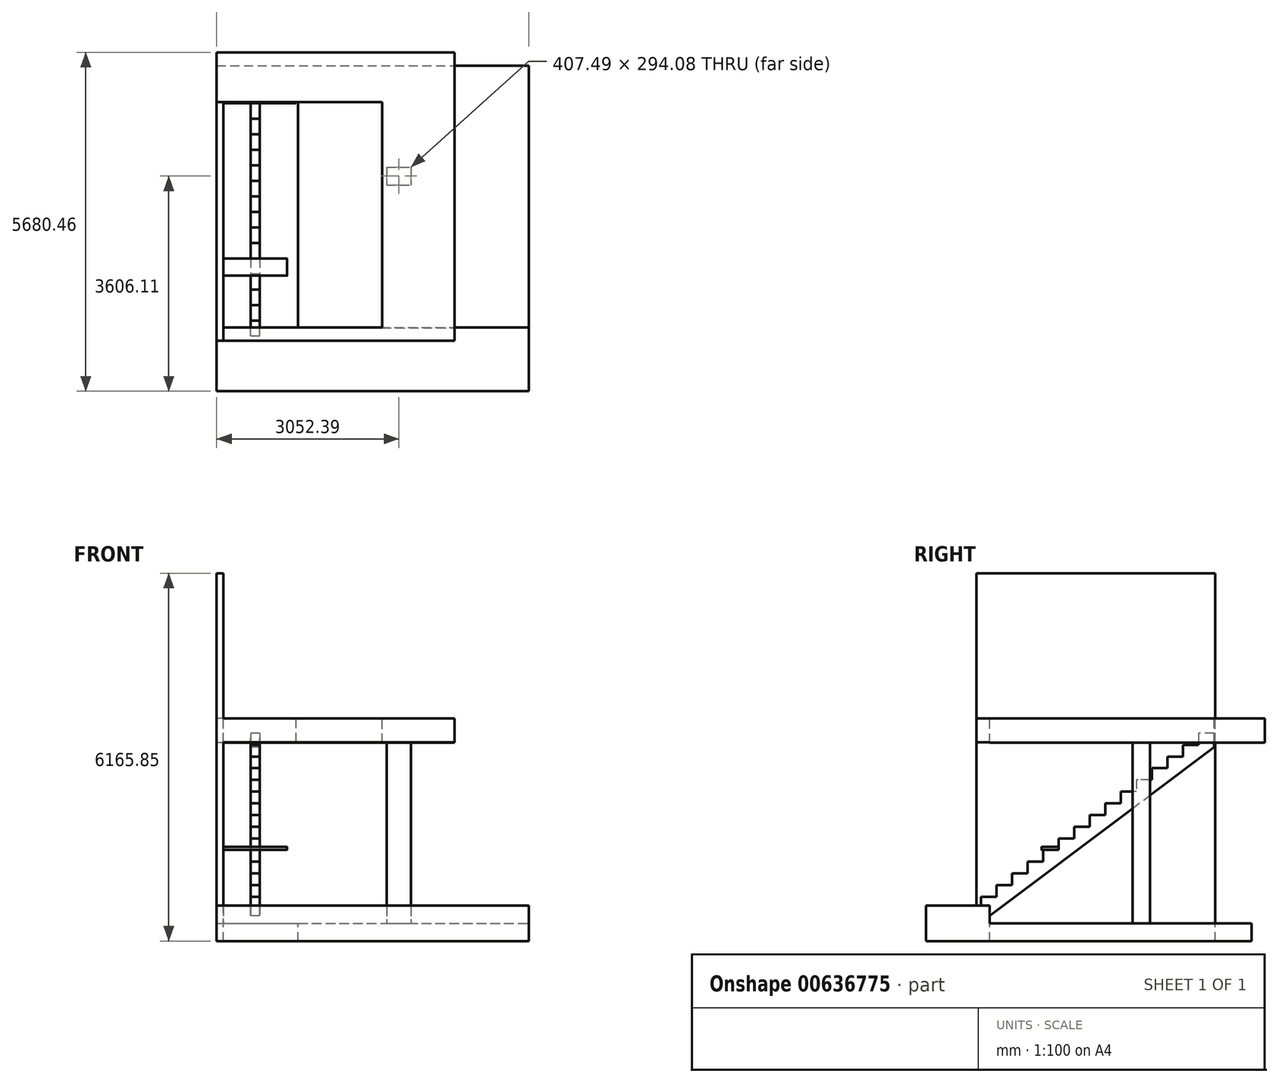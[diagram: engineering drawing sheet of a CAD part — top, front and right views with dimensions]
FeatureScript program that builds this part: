
annotation { "Feature Type Name" : "Feature", "Feature Type Description" : "" }
export const myFeature = defineFeature(function(context is Context, id is Id, definition is map)
    precondition{}
    {
        {
            var Q0;
            Q0=qCreatedBy(makeId("Top.planeOp"),FACE);
            var Q1;
            Q1 = qBodyType(qCreatedBy(id + "F1" ,EDGE), BodyType.WIRE);
            cPlane(context, id + "F0", {"entities" : qUnion([Q0, Q1]), "cplaneType" : CPlaneType.OFFSET, "offset" : 3432.17 * mm, "width" : 152.4 * mm, "height" : 152.4 * mm});
        }
        {
            var Q0;
            Q0=qCreatedBy(makeId("Top.planeOp"),FACE);
            var sketch = newSketch(context, id + "F1", { "sketchPlane" : qUnion([Q0])});
            skLineSegment(sketch, "E0.bottom", {"start": v(0, 0) * mm, "end": v(1250.95, 0) * mm});
            skLineSegment(sketch, "E0.top", {"start": v(0, 3778.25) * mm, "end": v(1250.95, 3778.25) * mm});
            skLineSegment(sketch, "E0.left", {"start": v(0, 0) * mm, "end": v(0, 3778.25) * mm});
            skLineSegment(sketch, "E0.right", {"start": v(1250.95, 0) * mm, "end": v(1250.95, 3778.25) * mm});
            skLineSegment(sketch, "E1.bottom", {"start": v(-114.3, -1066.8) * mm, "end": v(5114.93, -1066.8) * mm});
            skLineSegment(sketch, "E1.top", {"start": v(-114.3, 4387.85) * mm, "end": v(5114.93, 4387.85) * mm});
            skLineSegment(sketch, "E1.left", {"start": v(-114.3, -1066.8) * mm, "end": v(-114.3, 4387.85) * mm});
            skLineSegment(sketch, "E1.right", {"start": v(5114.93, -1066.8) * mm, "end": v(5114.93, 4387.85) * mm});
            skSolve(sketch);
        }
        {
            var Q0;
            Q0=makeQuery(id+"F1.imprint","IMPRINT",FACE,{"disambiguationData":[TD([[makeQuery(id+"F1.imprint","IMPRINT",EDGE,{"derivedFrom":sQuery(id+"F1.wireOp",EDGE,"E0.bottom")}),-1.0]])]});
            extrude(context, id + "F2", {"entities" : qUnion([Q0]), "oppositeDirection" : true, "depth" : 298.45 * mm, "offsetDistance" : 25.4 * mm});
        }
        {
            var Q0;
            Q0=makeQuery(id+"F1.imprint","IMPRINT",FACE,{"disambiguationData":[TD([[makeQuery(id+"F1.imprint","IMPRINT",EDGE,{"derivedFrom":sQuery(id+"F1.wireOp",EDGE,"E0.bottom")}),-1.0]])]});
            var sketch = newSketch(context, id + "F3", { "sketchPlane" : qUnion([Q0])});
            skLineSegment(sketch, "E2.bottom", {"start": v(-114.3, -1066.8) * mm, "end": v(5114.93, -1066.8) * mm});
            skLineSegment(sketch, "E2.top", {"start": v(-114.3, 0) * mm, "end": v(5114.93, 0) * mm});
            skLineSegment(sketch, "E2.left", {"start": v(-114.3, -1066.8) * mm, "end": v(-114.3, 0) * mm});
            skLineSegment(sketch, "E2.right", {"start": v(5114.93, -1066.8) * mm, "end": v(5114.93, 0) * mm});
            skSolve(sketch);
        }
        {
            var Q0;
            Q0=makeQuery(id+"F3.imprint","IMPRINT",FACE,{"disambiguationData":[TD([[makeQuery(id+"F3.imprint","IMPRINT",EDGE,{"derivedFrom":sQuery(id+"F3.wireOp",EDGE,"E2.bottom")}),1.0]])]});
            extrude(context, id + "F4", {"entities" : qUnion([Q0]), "operationType" : NewBodyOperationType.ADD, "depth" : 298.45 * mm, "offsetDistance" : 25.4 * mm});
        }
        {
            var Q0;
            Q0=qCreatedBy(id+"F0.planeOp",FACE);
            var sketch = newSketch(context, id + "F5", { "sketchPlane" : qUnion([Q0])});
            skLineSegment(sketch, "E3.top", {"start": v(0, 3778.25) * mm, "end": v(2660.65, 3778.25) * mm});
            skLineSegment(sketch, "E3.left", {"start": v(0, 0) * mm, "end": v(0, 3778.25) * mm});
            skLineSegment(sketch, "E4.bottom", {"start": v(-114.3, 0) * mm, "end": v(0, 0) * mm});
            skLineSegment(sketch, "E4.top", {"start": v(-114.3, 4613.66) * mm, "end": v(3863.97, 4613.66) * mm});
            skLineSegment(sketch, "E4.left", {"start": v(-114.3, 0) * mm, "end": v(-114.3, 4613.66) * mm});
            skLineSegment(sketch, "E5", {"start": v(2660.65, 3778.25) * mm, "end": v(2660.65, -1.59) * mm});
            skLineSegment(sketch, "E6", {"start": v(2660.65, -1.59) * mm, "end": v(3873.5, -1.59) * mm});
            skLineSegment(sketch, "E7", {"start": v(3873.5, -1.59) * mm, "end": v(3873.5, 4613.66) * mm});
            skLineSegment(sketch, "E8", {"start": v(3873.5, 4613.66) * mm, "end": v(3863.97, 4613.66) * mm});
            skSolve(sketch);
        }
        {
            var Q0;
            Q0 = qSketchRegion(id + "F5", true);
            extrude(context, id + "F6", {"entities" : qUnion([Q0]), "oppositeDirection" : true, "depth" : 404.8 * mm, "offsetDistance" : 25.4 * mm});
        }
        {
            var Q0;
            Q0=makeQuery(id+"F5.imprint","IMPRINT",FACE,{"disambiguationData":[TD([[makeQuery(id+"F5.imprint","IMPRINT",EDGE,{"derivedFrom":sQuery(id+"F5.wireOp",EDGE,"E3.top")}),1.0]])]});
            var sketch = newSketch(context, id + "F7", { "sketchPlane" : qUnion([Q0])});
            skLineSegment(sketch, "E9", {"start": v(-114.3, 0) * mm, "end": v(3873.5, 0) * mm});
            skLineSegment(sketch, "E10", {"start": v(3873.5, 0) * mm, "end": v(3873.5, -222.25) * mm});
            skLineSegment(sketch, "E11", {"start": v(3873.5, -222.25) * mm, "end": v(-114.3, -222.25) * mm});
            skLineSegment(sketch, "E12", {"start": v(-114.3, -222.25) * mm, "end": v(-114.3, 0) * mm});
            skSolve(sketch);
        }
        {
            var Q0;
            {var subQ2=sQuery(id+"F7.wireOp",EDGE,"E11");Q0=makeQuery(id+"F7.imprint","IMPRINT",FACE,{"disambiguationData":[TD([[makeQuery(id+"F7.imprint","IMPRINT",EDGE,{"derivedFrom":subQ2}),-1.0]])]});}
            extrude(context, id + "F8", {"entities" : qUnion([Q0]), "oppositeDirection" : true, "depth" : 400.05 * mm, "offsetDistance" : 25.4 * mm});
        }
        {
            var Q0;
            Q0=makeQuery(id+"F1.imprint","IMPRINT",FACE,{"disambiguationData":[TD([[makeQuery(id+"F1.imprint","IMPRINT",EDGE,{"derivedFrom":sQuery(id+"F1.wireOp",EDGE,"E0.bottom")}),-1.0]])]});
            var sketch = newSketch(context, id + "F9", { "sketchPlane" : qUnion([Q0])});
            skLineSegment(sketch, "E13.bottom", {"start": v(-114.3, 3778.25) * mm, "end": v(0, 3778.25) * mm});
            skLineSegment(sketch, "E13.top", {"start": v(-114.3, -222.25) * mm, "end": v(0, -222.25) * mm});
            skLineSegment(sketch, "E13.left", {"start": v(-114.3, 3778.25) * mm, "end": v(-114.3, -222.25) * mm});
            skLineSegment(sketch, "E13.right", {"start": v(0, 3778.25) * mm, "end": v(0, -222.25) * mm});
            skSolve(sketch);
        }
        {
            var Q0;
            Q0 = qSketchRegion(id + "F9", true);
            extrude(context, id + "F10", {"entities" : qUnion([Q0]), "operationType" : NewBodyOperationType.ADD, "depth" : 5867.4 * mm, "offsetDistance" : 25.4 * mm});
        }
        {
            var Q0;
            Q0=makeQuery(id+"F5.imprint","IMPRINT",FACE,{"disambiguationData":[TD([[makeQuery(id+"F5.imprint","IMPRINT",EDGE,{"derivedFrom":sQuery(id+"F5.wireOp",EDGE,"E3.top")}),1.0]])]});
            var sketch = newSketch(context, id + "F11", { "sketchPlane" : qUnion([Q0])});
            skLineSegment(sketch, "E14.bottom", {"start": v(0, 3778.25) * mm, "end": v(1219.2, 3778.25) * mm});
            skLineSegment(sketch, "E14.top", {"start": v(0, 3759.2) * mm, "end": v(1219.2, 3759.2) * mm});
            skLineSegment(sketch, "E14.left", {"start": v(0, 3778.25) * mm, "end": v(0, 3759.2) * mm});
            skLineSegment(sketch, "E14.right", {"start": v(1219.2, 3778.25) * mm, "end": v(1219.2, 3759.2) * mm});
            skSolve(sketch);
        }
        {
            var Q0;
            Q0 = qSketchRegion(id + "F11", true);
            extrude(context, id + "F12", {"entities" : qUnion([Q0]), "oppositeDirection" : true, "depth" : 391.16 * mm, "offsetDistance" : 25.4 * mm});
        }
        {
            var Q0;
            Q0=makeQuery(id+"F10.opExtrude","SWEPT_FACE",FACE,{"disambiguationData":[OSD([sQuery(id+"F9.wireOp",EDGE,"E13.right")])]});
            cPlane(context, id + "F13", {"entities" : qUnion([Q0]), "cplaneType" : CPlaneType.OFFSET, "offset" : 457.2 * mm, "width" : 152.4 * mm, "height" : 152.4 * mm});
        }
        {
            var Q0;
            Q0=qCreatedBy(id+"F13.planeOp",FACE);
            var sketch = newSketch(context, id + "F14", { "sketchPlane" : qUnion([Q0])});
            skLineSegment(sketch, "E15", {"start": v(3759.2, 3185.52) * mm, "end": v(3498.85, 3185.52) * mm});
            skLineSegment(sketch, "E16", {"start": v(3498.85, 3185.52) * mm, "end": v(3498.85, 2989.66) * mm});
            skLineSegment(sketch, "E17", {"start": v(3498.85, 2989.66) * mm, "end": v(3238.5, 2989.66) * mm});
            skLineSegment(sketch, "E18", {"start": v(3238.5, 2989.66) * mm, "end": v(3238.5, 2793.8) * mm});
            skLineSegment(sketch, "E19", {"start": v(3238.5, 2793.8) * mm, "end": v(2978.15, 2793.8) * mm});
            skLineSegment(sketch, "E20", {"start": v(2978.15, 2793.8) * mm, "end": v(2978.15, 2597.94) * mm});
            skLineSegment(sketch, "E21", {"start": v(2978.15, 2597.94) * mm, "end": v(2717.8, 2597.94) * mm});
            skLineSegment(sketch, "E22", {"start": v(2717.8, 2597.94) * mm, "end": v(2717.8, 2402.09) * mm});
            skLineSegment(sketch, "E23", {"start": v(2717.8, 2402.09) * mm, "end": v(2457.45, 2402.09) * mm});
            skLineSegment(sketch, "E24", {"start": v(2457.45, 2402.09) * mm, "end": v(2457.45, 2206.23) * mm});
            skLineSegment(sketch, "E25", {"start": v(2457.45, 2206.23) * mm, "end": v(2197.1, 2206.23) * mm});
            skLineSegment(sketch, "E26", {"start": v(2197.1, 2206.23) * mm, "end": v(2197.1, 2010.37) * mm});
            skLineSegment(sketch, "E27", {"start": v(2197.1, 2010.37) * mm, "end": v(1936.75, 2010.37) * mm});
            skLineSegment(sketch, "E28", {"start": v(1936.75, 2010.37) * mm, "end": v(1936.75, 1814.51) * mm});
            skLineSegment(sketch, "E29", {"start": v(1936.75, 1814.51) * mm, "end": v(1676.4, 1814.51) * mm});
            skLineSegment(sketch, "E30", {"start": v(1676.4, 1814.51) * mm, "end": v(1676.4, 1618.65) * mm});
            skLineSegment(sketch, "E31", {"start": v(1676.4, 1618.65) * mm, "end": v(1416.05, 1618.65) * mm});
            skLineSegment(sketch, "E32", {"start": v(1416.05, 1618.65) * mm, "end": v(1416.05, 1422.8) * mm});
            skLineSegment(sketch, "E33", {"start": v(1416.05, 1422.8) * mm, "end": v(1155.7, 1422.8) * mm});
            skLineSegment(sketch, "E34", {"start": v(1155.7, 1422.8) * mm, "end": v(1155.7, 1226.94) * mm});
            skLineSegment(sketch, "E35", {"start": v(1155.7, 1226.94) * mm, "end": v(895.35, 1226.94) * mm});
            skLineSegment(sketch, "E36", {"start": v(895.35, 1226.94) * mm, "end": v(895.35, 1031.08) * mm});
            skLineSegment(sketch, "E37", {"start": v(895.35, 1031.08) * mm, "end": v(635, 1031.08) * mm});
            skLineSegment(sketch, "E38", {"start": v(635, 1031.08) * mm, "end": v(635, 835.22) * mm});
            skLineSegment(sketch, "E39", {"start": v(635, 835.22) * mm, "end": v(374.65, 835.22) * mm});
            skLineSegment(sketch, "E40", {"start": v(0, 124.28) * mm, "end": v(3759.2, 2952.28) * mm});
            skLineSegment(sketch, "E41", {"start": v(3759.2, 2952.28) * mm, "end": v(3759.2, 3185.52) * mm});
            skLineSegment(sketch, "E42", {"start": v(374.65, 835.22) * mm, "end": v(374.65, 639.37) * mm});
            skLineSegment(sketch, "E43", {"start": v(374.65, 639.37) * mm, "end": v(114.3, 639.37) * mm});
            skLineSegment(sketch, "E44", {"start": v(114.3, 639.37) * mm, "end": v(114.3, 443.5) * mm});
            skLineSegment(sketch, "E45", {"start": v(374.65, 835.22) * mm, "end": v(635, 1031.08) * mm, "construction": true});
            skLineSegment(sketch, "E46", {"start": v(-146.05, 443.5) * mm, "end": v(114.3, 443.5) * mm});
            skLineSegment(sketch, "E47", {"start": v(-146.05, 443.5) * mm, "end": v(-146.05, 298.45) * mm});
            skLineSegment(sketch, "E48", {"start": v(-146.05, 298.45) * mm, "end": v(0, 298.45) * mm});
            skLineSegment(sketch, "E49", {"start": v(0, 298.45) * mm, "end": v(0, 124.28) * mm});
            skLineSegment(sketch, "E50", {"start": v(3463.92, 3432.18) * mm, "end": v(3463.92, 3236.32) * mm, "construction": true});
            skLineSegment(sketch, "E51", {"start": v(3463.92, 3236.32) * mm, "end": v(3463.92, 3185.52) * mm, "construction": true});
            skLineSegment(sketch, "E52", {"start": v(-283.8, 494.3) * mm, "end": v(-283.8, 298.45) * mm, "construction": true});
            skSolve(sketch);
        }
        {
            var Q0;
            Q0=makeQuery(id+"F14.imprint","IMPRINT",FACE,{"disambiguationData":[TD([[makeQuery(id+"F14.imprint","IMPRINT",EDGE,{"derivedFrom":sQuery(id+"F14.wireOp",EDGE,"E15")}),1.0]])]});
            extrude(context, id + "F15", {"entities" : qUnion([Q0]), "depth" : 152.4 * mm, "offsetDistance" : 25.4 * mm});
        }
        {
            var Q0;
            Q0=makeQuery(id+"F1.imprint","IMPRINT",FACE,{"disambiguationData":[TD([[makeQuery(id+"F1.imprint","IMPRINT",EDGE,{"derivedFrom":sQuery(id+"F1.wireOp",EDGE,"E0.bottom")}),-1.0]])]});
            var sketch = newSketch(context, id + "F16", { "sketchPlane" : qUnion([Q0])});
            skLineSegment(sketch, "E53.bottom", {"start": v(2734.34, 2686.35) * mm, "end": v(3141.84, 2686.35) * mm});
            skLineSegment(sketch, "E53.top", {"start": v(2734.34, 2392.27) * mm, "end": v(3141.84, 2392.27) * mm});
            skLineSegment(sketch, "E53.left", {"start": v(2734.34, 2686.35) * mm, "end": v(2734.34, 2392.27) * mm});
            skLineSegment(sketch, "E53.right", {"start": v(3141.84, 2686.35) * mm, "end": v(3141.84, 2392.27) * mm});
            skSolve(sketch);
        }
        {
            var Q0;
            Q0 = qSketchRegion(id + "F16", true);
            var Q1;
            Q1=makeQuery(id+"F6.opExtrude","CAP_VERTEX",VERTEX,{"disambiguationData":[OSD([sQuery(id+"F5.wireOp",EDGE,"E7"),sQuery(id+"F5.wireOp",EDGE,"E8")])],"isStart":false});
            extrude(context, id + "F17", {"entities" : qUnion([Q0]), "operationType" : NewBodyOperationType.ADD, "endBound" : BoundingType.UP_TO_VERTEX, "depth" : 25.4 * mm, "endBoundEntityVertex" : qUnion([Q1]), "offsetDistance" : 25.4 * mm});
        }
        {
            var Q0;
            Q0=makeQuery(id+"F15.opExtrude","CAP_FACE",FACE,{"disambiguationData":[OSD([sQuery(id+"F14.wireOp",EDGE,"E15"),sQuery(id+"F14.wireOp",EDGE,"E16"),sQuery(id+"F14.wireOp",EDGE,"E17"),sQuery(id+"F14.wireOp",EDGE,"E18"),sQuery(id+"F14.wireOp",EDGE,"E19"),sQuery(id+"F14.wireOp",EDGE,"E20"),sQuery(id+"F14.wireOp",EDGE,"E21"),sQuery(id+"F14.wireOp",EDGE,"E22"),sQuery(id+"F14.wireOp",EDGE,"E23"),sQuery(id+"F14.wireOp",EDGE,"E24"),sQuery(id+"F14.wireOp",EDGE,"E25"),sQuery(id+"F14.wireOp",EDGE,"E26"),sQuery(id+"F14.wireOp",EDGE,"E27"),sQuery(id+"F14.wireOp",EDGE,"E28"),sQuery(id+"F14.wireOp",EDGE,"E29"),sQuery(id+"F14.wireOp",EDGE,"E30"),sQuery(id+"F14.wireOp",EDGE,"E31"),sQuery(id+"F14.wireOp",EDGE,"E32"),sQuery(id+"F14.wireOp",EDGE,"E33"),sQuery(id+"F14.wireOp",EDGE,"E34"),sQuery(id+"F14.wireOp",EDGE,"E35"),sQuery(id+"F14.wireOp",EDGE,"E36"),sQuery(id+"F14.wireOp",EDGE,"E37"),sQuery(id+"F14.wireOp",EDGE,"E38"),sQuery(id+"F14.wireOp",EDGE,"E39"),sQuery(id+"F14.wireOp",EDGE,"E40"),sQuery(id+"F14.wireOp",EDGE,"E41"),sQuery(id+"F14.wireOp",EDGE,"E42"),sQuery(id+"F14.wireOp",EDGE,"E43"),sQuery(id+"F14.wireOp",EDGE,"E44"),sQuery(id+"F14.wireOp",EDGE,"E46"),sQuery(id+"F14.wireOp",EDGE,"E47"),sQuery(id+"F14.wireOp",EDGE,"E48"),sQuery(id+"F14.wireOp",EDGE,"E49")])],"isStart":false});
            var Q1;
            Q1=makeQuery(id+"F15.opExtrude","CAP_FACE",FACE,{"disambiguationData":[OSD([sQuery(id+"F14.wireOp",EDGE,"E15"),sQuery(id+"F14.wireOp",EDGE,"E16"),sQuery(id+"F14.wireOp",EDGE,"E17"),sQuery(id+"F14.wireOp",EDGE,"E18"),sQuery(id+"F14.wireOp",EDGE,"E19"),sQuery(id+"F14.wireOp",EDGE,"E20"),sQuery(id+"F14.wireOp",EDGE,"E21"),sQuery(id+"F14.wireOp",EDGE,"E22"),sQuery(id+"F14.wireOp",EDGE,"E23"),sQuery(id+"F14.wireOp",EDGE,"E24"),sQuery(id+"F14.wireOp",EDGE,"E25"),sQuery(id+"F14.wireOp",EDGE,"E26"),sQuery(id+"F14.wireOp",EDGE,"E27"),sQuery(id+"F14.wireOp",EDGE,"E28"),sQuery(id+"F14.wireOp",EDGE,"E29"),sQuery(id+"F14.wireOp",EDGE,"E30"),sQuery(id+"F14.wireOp",EDGE,"E31"),sQuery(id+"F14.wireOp",EDGE,"E32"),sQuery(id+"F14.wireOp",EDGE,"E33"),sQuery(id+"F14.wireOp",EDGE,"E34"),sQuery(id+"F14.wireOp",EDGE,"E35"),sQuery(id+"F14.wireOp",EDGE,"E36"),sQuery(id+"F14.wireOp",EDGE,"E37"),sQuery(id+"F14.wireOp",EDGE,"E38"),sQuery(id+"F14.wireOp",EDGE,"E39"),sQuery(id+"F14.wireOp",EDGE,"E40"),sQuery(id+"F14.wireOp",EDGE,"E41"),sQuery(id+"F14.wireOp",EDGE,"E42"),sQuery(id+"F14.wireOp",EDGE,"E43"),sQuery(id+"F14.wireOp",EDGE,"E44"),sQuery(id+"F14.wireOp",EDGE,"E46"),sQuery(id+"F14.wireOp",EDGE,"E47"),sQuery(id+"F14.wireOp",EDGE,"E48"),sQuery(id+"F14.wireOp",EDGE,"E49")])],"isStart":true});
            cPlane(context, id + "F18", {"entities" : qUnion([Q0, Q1]), "cplaneType" : CPlaneType.MID_PLANE, "offset" : 25.4 * mm, "width" : 152.4 * mm, "height" : 152.4 * mm});
        }
        {
            var Q0;
            Q0=qCreatedBy(id+"F18.planeOp",FACE);
            var sketch = newSketch(context, id + "F19", { "sketchPlane" : qUnion([Q0])});
            skLineSegment(sketch, "E54.bottom", {"start": v(1155.7, 1226.94) * mm, "end": v(876.3, 1226.94) * mm});
            skLineSegment(sketch, "E54.top", {"start": v(1155.7, 1277.74) * mm, "end": v(876.3, 1277.74) * mm});
            skLineSegment(sketch, "E54.left", {"start": v(1155.7, 1226.94) * mm, "end": v(1155.7, 1277.74) * mm});
            skLineSegment(sketch, "E54.right", {"start": v(869.95, 1233.29) * mm, "end": v(869.95, 1271.39) * mm});
            skPoint(sketch, "E55.visualSharp", {"position": v(869.95, 1277.74) * mm});
            skArc(sketch, "E55.filletArc", {"start": v(876.3, 1277.74) * mm, "mid": v(871.8, 1275.88) * mm, "end": v(869.95, 1271.39) * mm});
            skPoint(sketch, "E56.visualSharp", {"position": v(869.95, 1226.94) * mm});
            skArc(sketch, "E56.filletArc", {"start": v(869.95, 1233.29) * mm, "mid": v(871.8, 1228.8) * mm, "end": v(876.3, 1226.94) * mm});
            skSolve(sketch);
        }
        {
            var Q0;
            Q0 = qSketchRegion(id + "F19", true);
            extrude(context, id + "F20", {"entities" : qUnion([Q0]), "endBound" : BoundingType.SYMMETRIC, "depth" : 1066.8 * mm, "offsetDistance" : 25.4 * mm});
        }
        {
            var Q0;
            Q0=makeQuery(id+"F20.opExtrude","CAP_EDGE",EDGE,{"disambiguationData":[OSD([sQuery(id+"F19.wireOp",EDGE,"E54.top")])],"isStart":false});
            var Q1;
            Q1=makeQuery(id+"F20.opExtrude","CAP_EDGE",EDGE,{"disambiguationData":[OSD([sQuery(id+"F19.wireOp",EDGE,"E54.bottom")])],"isStart":false});
            var Q2;
            Q2=makeQuery(id+"F20.opExtrude","CAP_EDGE",EDGE,{"disambiguationData":[OSD([sQuery(id+"F19.wireOp",EDGE,"E54.top")])],"isStart":true});
            var Q3;
            Q3=makeQuery(id+"F20.opExtrude","CAP_EDGE",EDGE,{"disambiguationData":[OSD([sQuery(id+"F19.wireOp",EDGE,"E54.bottom")])],"isStart":true});
            fillet(context, id + "F21", {"entities" : qUnion([Q0, Q1, Q2, Q3]), "radius" : 6.35 * mm, "allowEdgeOverflow" : false});
        }
    });
